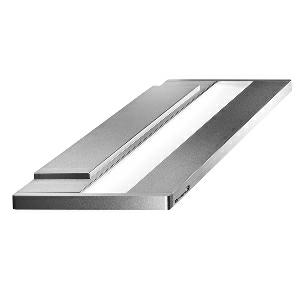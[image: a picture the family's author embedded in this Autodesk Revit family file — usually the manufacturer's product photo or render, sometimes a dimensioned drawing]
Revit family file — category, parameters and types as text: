
# Revit family: zera_bed_-_zew_11000_830_-_ul_li_nl_00813008_5e2e
name_source: partatom
category: Lighting Fixtures
units: mm (PartAtom-declared; Revit-internal decimal feet)

## family parameters
Cut with Voids When Loaded = No
Host = Face
Light Source = No
Part Type = Normal
Room Calculation Point = No
Round Connector Dimension = Use Diameter
Shared = No

## types (1)
- AL+UL (1 x LED, 9800 lm, 4000K/3000K)
    Apparent Load = 109 VA
    Approval mark = CE
    CIE Flux Codes = 45 81 99 47 100
    Color Rendering = 90/80
    Color Temperature = 4000K/3000K
    Default Elevation = 2000 mm  [stored 6.56168 ft]
    Description = ZEW 11000/830|Wall-mounted luminaire|light source:   Warm white   |work equipment: Power supply unit|luminous flux: 10890 lm|light distribution: Direct/indirect|class of protection: I|technology: Switchable|mains lead: Connector 5 pin|glare control: Diffusor|special features: General light, indirect, 3000K, Ra80, DIN EN 60598-2-25, Reading light, direct, 2700K, Ra90, indir, Switch left, dir 4K 60W Ra95|
    Frequency = 50 Hz, 60 Hz
    Height = 20 mm  [stored 0.0656168 ft]
    Lamp = 1 x LED
    Lamp Light Flux = 9800 lm
    Lamp count = 1
    Length = 1050 mm
    Luminous efficacy = 90 lm/W
    Manufacturer = Waldmann
    ModVariant = No
    Model = 00813008
    Mounting Place = Wall
    Mounting Type = Surface mounted
    Number of Poles = 1
    OnlyDefault = Yes
    Power Factor = 1
    Product Name = ZERA.bed - ZEW 11000/830 - UL LI/NL
    Product group = Wall mounted Luminaire
    ProductGroupID = 20
    Protection Class = Protection class I
    Protection Degree = IP 20
    RLX_Detail_Level = 1
    RLX_Emergency_Light_Flux = 0 lm
    RLX_Emergency_Type = 0
    RLX_Emergency_Type_DB = No
    RlxData = <blob elided: 60169 chars, md5=50e0f2ce>
    Socket = socket
    Standby Power = 0 W
    System Light Flux = 9800 lm
    System Power = 109 W
    Type Comments = General and Examation Light
    Type Image = zera_bed.jpg
    URL = http://relux.com
    VarID = al_ul_37f9
    Voltage = 230 V
    Voltage Range = 220-240 V
    Weight = 0.00 kg
    Width = 230 mm

note: [stored X ft] marks values corroborated as IEEE doubles in the binary element streams (Revit-internal decimal feet)

## geometry (parser evidence)
native form markers: Blend x4, Sweep x14
no freeform markers — native parametric forms only
